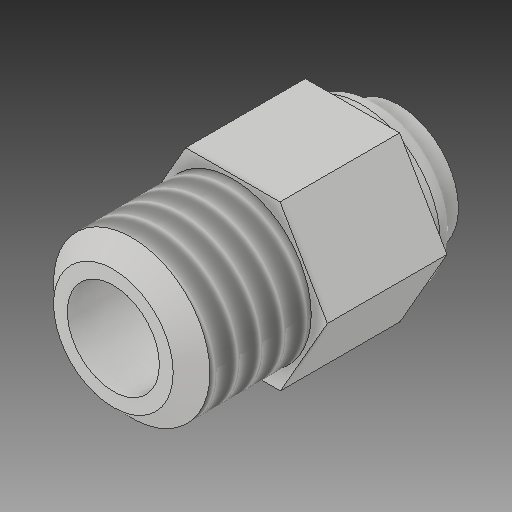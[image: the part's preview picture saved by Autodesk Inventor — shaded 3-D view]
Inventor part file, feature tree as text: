
AUTODESK INVENTOR PART (.ipt)
format: ipt  version: 2018 (Build 220112000, 112)  size: 176,128 bytes
history: native  units: mm
features: sketch x6, other x3
ambient origin geometry x8: Origin, YZ Plane, XZ Plane, XY Plane, X Axis, Y Axis, Z Axis, Center Point
bodies: Solid1 (feature_tree)
feature tree (9):
  other  "Pushfit-Adapter.ipt"
  other  "Solid1::Pushfit-Adapter.ipt"
  other  "TaggingFeature1"
  sketch  "Sketch1"  dims[d0=10.0mm]
  sketch  "Sketch2"
  sketch  "Sketch3"
  sketch  "Sketch4"
  sketch  "Sketch5"
  sketch  "Sketch6"
